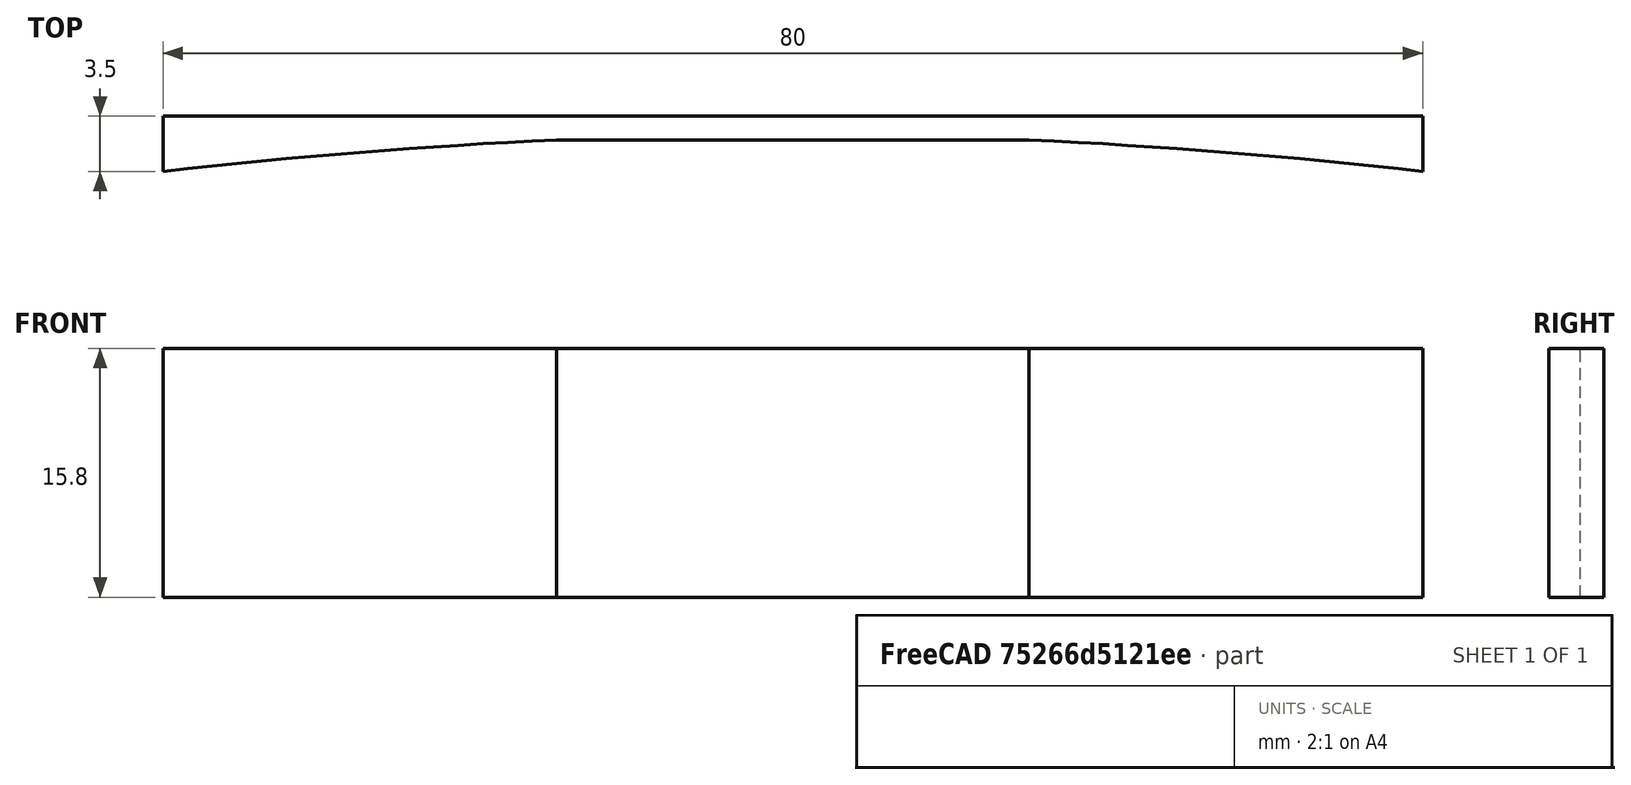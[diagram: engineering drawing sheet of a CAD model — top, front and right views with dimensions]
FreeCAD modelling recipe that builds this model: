
FCSTD DOCUMENT  (FreeCAD 0.16R6707 (Git))
Label: C920-back
License: All rights reserved
LicenseURL: http://en.wikipedia.org/wiki/All_rights_reserved
objects: Sketcher::SketchObject×1, PartDesign::Pad×1
note: 3 computed .brp shape members not serialized (recipe doc carries the construction recipe); baked Part::Feature solids carry a one-line shape summary decoded from their .brp

FEATURE [Sketcher::SketchObject] Sketch
  sketch-geometry (8):
    g0: LineSegment StartX=-15 StartY=50 StartZ=0 EndX=15 EndY=50 EndZ=0
    g1: LineSegment [constr] StartX=30 StartY=49 StartZ=0 EndX=40 EndY=48 EndZ=0
    g2: ArcOfCircle CenterX=-2.7 CenterY=-328.5 CenterZ=0 NormalX=0 NormalY=0 NormalZ=1 Radius=378.914 StartAngle=1.45787 EndAngle=1.52407
    g3: LineSegment [constr] StartX=-30 StartY=49 StartZ=0 EndX=-40 EndY=48 EndZ=0
    g4: ArcOfCircle CenterX=2.7 CenterY=-328.5 CenterZ=0 NormalX=0 NormalY=0 NormalZ=1 Radius=378.914 StartAngle=1.61753 EndAngle=1.68373
    g5: LineSegment StartX=-40 StartY=48 StartZ=0 EndX=-40 EndY=51.5 EndZ=0
    g6: LineSegment StartX=-40 StartY=51.5 StartZ=0 EndX=40 EndY=51.5 EndZ=0
    g7: LineSegment StartX=40 StartY=51.5 StartZ=0 EndX=40 EndY=48 EndZ=0
  constraints (24):
    c: Horizontal(g0)
    c: Symmetric(g0,g0,g-2)
    c: DistanceX(g-1,g0) = 15
    c: DistanceY(g-1,g0) = 50
    c: DistanceX(g-1,g1) = 30
    c: DistanceY(g-1,g1) = 49
    c: DistanceY(g-1,g1) = 48
    c: DistanceX(g-1,g1) = 40
    c: Coincident(g2,g1)
    c: PointOnObject(g1,g2)
    c: Coincident(g2,g0)
    c: Symmetric(g3,g1,g-2)
    c: Symmetric(g3,g1,g-2)
    c: Coincident(g4,g0)
    c: Coincident(g4,g3)
    c: PointOnObject(g3,g4)
    c: Coincident(g5,g3)
    c: Vertical(g5)
    c: Coincident(g6,g5)
    c: Horizontal(g6)
    c: Coincident(g7,g6)
    c: Coincident(g7,g1)
    c: Vertical(g7)
    c: DistanceY(g-1,g5) = 51.5
FEATURE [PartDesign::Pad] Pad
  Length = 15.8
  Length2 = 100
  Sketch = -> Sketch
  Type = 0
